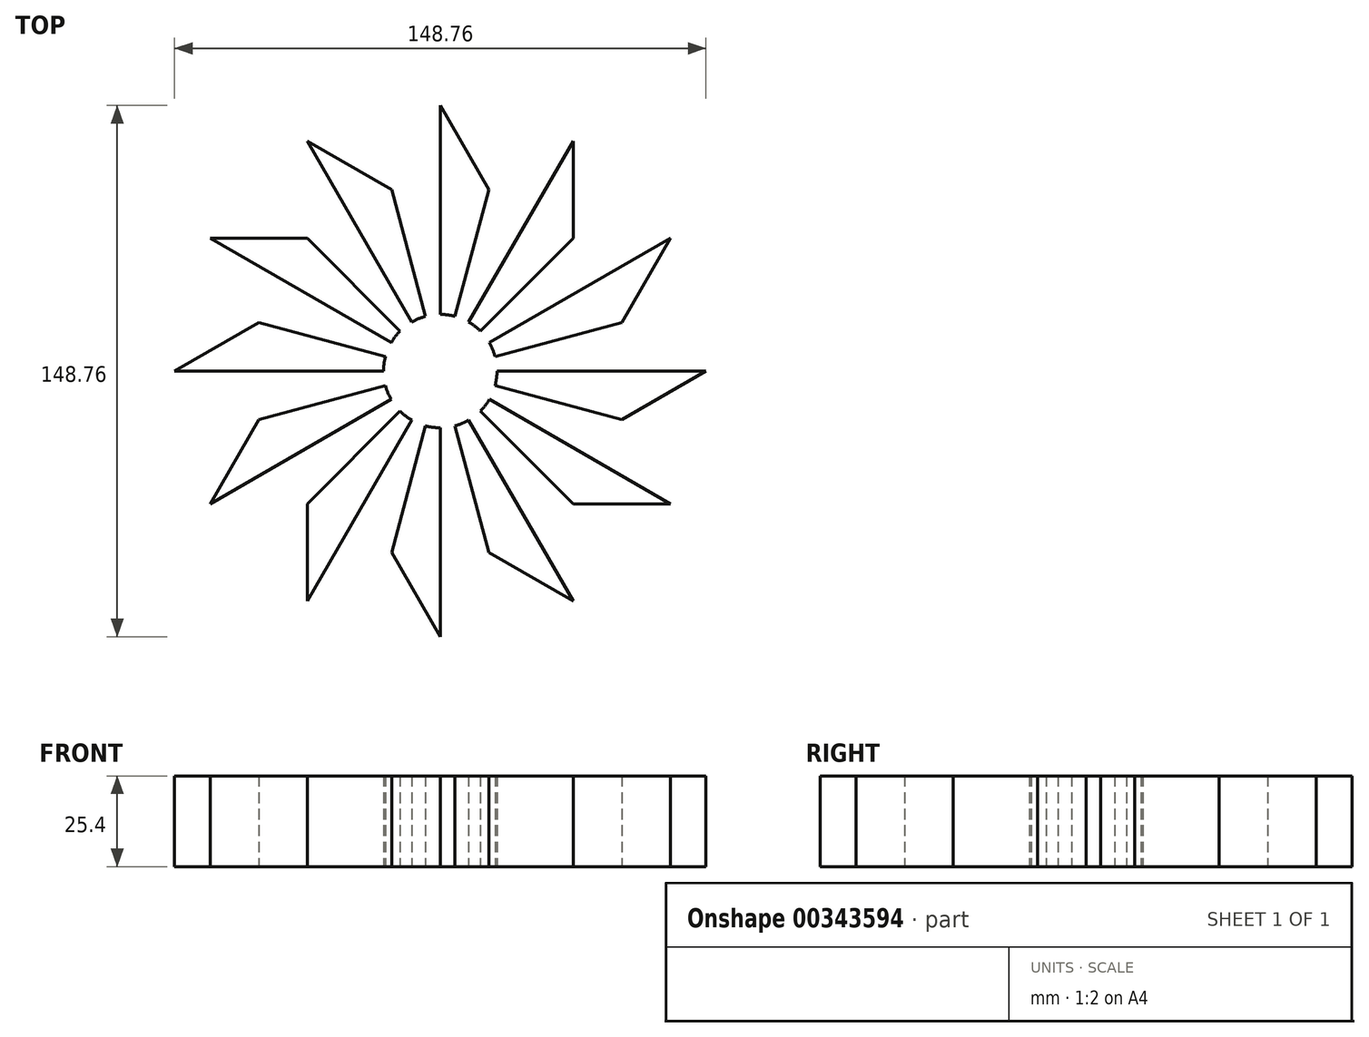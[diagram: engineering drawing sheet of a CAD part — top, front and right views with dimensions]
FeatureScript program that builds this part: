
annotation { "Feature Type Name" : "Feature", "Feature Type Description" : "" }
export const myFeature = defineFeature(function(context is Context, id is Id, definition is map)
    precondition{}
    {
        {
            var Q0;
            Q0=qCreatedBy(makeId("Top.planeOp"),FACE);
            var sketch = newSketch(context, id + "F0", { "sketchPlane" : qUnion([Q0])});
            skLineSegment(sketch, "E0", {"start": v(15.33, 4.1) * mm, "end": v(50.8, 13.61) * mm});
            skLineSegment(sketch, "E1", {"start": v(50.8, 13.61) * mm, "end": v(74.38, 0) * mm});
            skLineSegment(sketch, "E2.MirrorCS", {"start": v(50.8, -13.61) * mm, "end": v(74.38, 0) * mm});
            skLineSegment(sketch, "E3", {"start": v(15.87, 0) * mm, "end": v(74.38, 0) * mm});
            skLineSegment(sketch, "E4.1.0", {"start": v(50.8, 13.61) * mm, "end": v(64.41, 37.19) * mm});
            skLineSegment(sketch, "E4.1.1", {"start": v(13.75, 7.94) * mm, "end": v(64.41, 37.19) * mm});
            skLineSegment(sketch, "E4.1.2", {"start": v(37.19, 37.19) * mm, "end": v(64.41, 37.19) * mm});
            skLineSegment(sketch, "E4.1.3", {"start": v(11.23, 11.23) * mm, "end": v(37.19, 37.19) * mm});
            skLineSegment(sketch, "E4.2.0", {"start": v(37.19, 37.19) * mm, "end": v(37.19, 64.41) * mm});
            skLineSegment(sketch, "E4.2.1", {"start": v(7.94, 13.75) * mm, "end": v(37.19, 64.41) * mm});
            skLineSegment(sketch, "E4.2.2", {"start": v(13.61, 50.8) * mm, "end": v(37.19, 64.41) * mm});
            skLineSegment(sketch, "E4.2.3", {"start": v(4.1, 15.33) * mm, "end": v(13.61, 50.8) * mm});
            skLineSegment(sketch, "E4.3.0", {"start": v(13.61, 50.8) * mm, "end": v(0, 74.38) * mm});
            skLineSegment(sketch, "E4.3.1", {"start": v(0, 15.87) * mm, "end": v(0, 74.38) * mm});
            skLineSegment(sketch, "E4.3.2", {"start": v(-13.61, 50.8) * mm, "end": v(0, 74.38) * mm});
            skLineSegment(sketch, "E4.3.3", {"start": v(-4.1, 15.33) * mm, "end": v(-13.61, 50.8) * mm});
            skLineSegment(sketch, "E4.4.0", {"start": v(-13.61, 50.8) * mm, "end": v(-37.19, 64.41) * mm});
            skLineSegment(sketch, "E4.4.1", {"start": v(-7.94, 13.75) * mm, "end": v(-37.19, 64.41) * mm});
            skLineSegment(sketch, "E4.4.2", {"start": v(-37.19, 37.19) * mm, "end": v(-37.19, 64.41) * mm});
            skLineSegment(sketch, "E4.4.3", {"start": v(-11.23, 11.23) * mm, "end": v(-37.19, 37.19) * mm});
            skLineSegment(sketch, "E4.5.0", {"start": v(-37.19, 37.19) * mm, "end": v(-64.41, 37.19) * mm});
            skLineSegment(sketch, "E4.5.1", {"start": v(-13.75, 7.94) * mm, "end": v(-64.41, 37.19) * mm});
            skLineSegment(sketch, "E4.5.2", {"start": v(-50.8, 13.61) * mm, "end": v(-64.41, 37.19) * mm});
            skLineSegment(sketch, "E4.5.3", {"start": v(-15.33, 4.1) * mm, "end": v(-50.8, 13.61) * mm});
            skLineSegment(sketch, "E4.6.0", {"start": v(-50.8, 13.61) * mm, "end": v(-74.38, 0) * mm});
            skLineSegment(sketch, "E4.6.1", {"start": v(-15.88, 0) * mm, "end": v(-74.38, 0) * mm});
            skLineSegment(sketch, "E4.6.2", {"start": v(-50.8, -13.61) * mm, "end": v(-74.38, 0) * mm});
            skLineSegment(sketch, "E4.6.3", {"start": v(-15.33, -4.1) * mm, "end": v(-50.8, -13.61) * mm});
            skLineSegment(sketch, "E4.7.0", {"start": v(-50.8, -13.61) * mm, "end": v(-64.41, -37.19) * mm});
            skLineSegment(sketch, "E4.7.1", {"start": v(-13.75, -7.94) * mm, "end": v(-64.41, -37.19) * mm});
            skLineSegment(sketch, "E4.7.2", {"start": v(-37.19, -37.19) * mm, "end": v(-64.41, -37.19) * mm});
            skLineSegment(sketch, "E4.7.3", {"start": v(-11.23, -11.23) * mm, "end": v(-37.19, -37.19) * mm});
            skLineSegment(sketch, "E4.8.0", {"start": v(-37.19, -37.19) * mm, "end": v(-37.19, -64.41) * mm});
            skLineSegment(sketch, "E4.8.1", {"start": v(-7.94, -13.75) * mm, "end": v(-37.19, -64.41) * mm});
            skLineSegment(sketch, "E4.8.2", {"start": v(-13.61, -50.8) * mm, "end": v(-37.19, -64.41) * mm});
            skLineSegment(sketch, "E4.8.3", {"start": v(-4.1, -15.33) * mm, "end": v(-13.61, -50.8) * mm});
            skLineSegment(sketch, "E4.9.0", {"start": v(-13.61, -50.8) * mm, "end": v(0, -74.38) * mm});
            skLineSegment(sketch, "E4.9.1", {"start": v(0, -15.88) * mm, "end": v(0, -74.38) * mm});
            skLineSegment(sketch, "E4.9.2", {"start": v(13.61, -50.8) * mm, "end": v(0, -74.38) * mm});
            skLineSegment(sketch, "E4.9.3", {"start": v(4.1, -15.33) * mm, "end": v(13.61, -50.8) * mm});
            skLineSegment(sketch, "E4.10.0", {"start": v(13.61, -50.8) * mm, "end": v(37.19, -64.41) * mm});
            skLineSegment(sketch, "E4.10.1", {"start": v(7.94, -13.75) * mm, "end": v(37.19, -64.41) * mm});
            skLineSegment(sketch, "E4.10.2", {"start": v(37.19, -37.19) * mm, "end": v(37.19, -64.41) * mm});
            skLineSegment(sketch, "E4.10.3", {"start": v(11.23, -11.23) * mm, "end": v(37.19, -37.19) * mm});
            skLineSegment(sketch, "E4.11.0", {"start": v(37.19, -37.19) * mm, "end": v(64.41, -37.19) * mm});
            skLineSegment(sketch, "E4.11.1", {"start": v(13.75, -7.94) * mm, "end": v(64.41, -37.19) * mm});
            skLineSegment(sketch, "E4.11.2", {"start": v(50.8, -13.61) * mm, "end": v(64.41, -37.19) * mm});
            skLineSegment(sketch, "E4.11.3", {"start": v(15.33, -4.1) * mm, "end": v(50.8, -13.61) * mm});
            skPoint(sketch, "E4.center", {"position": v(0, 0) * mm});
            skCircle(sketch, "E5", {"center": v(0, 0) * mm, "radius": 15.88 * mm});
            skSolve(sketch);
        }
        {
            var Q0;
            {var subQ0=sQuery(id+"F0.wireOp",EDGE,"E4.4.3");Q0=makeQuery(id+"F0.imprint","IMPRINT",FACE,{"disambiguationData":[TD([[makeQuery(id+"F0.imprint","IMPRINT",EDGE,{"derivedFrom":subQ0}),1.0]])]});}
            var Q1;
            {var subQ0=sQuery(id+"F0.wireOp",EDGE,"E4.3.3");Q1=makeQuery(id+"F0.imprint","IMPRINT",FACE,{"disambiguationData":[TD([[makeQuery(id+"F0.imprint","IMPRINT",EDGE,{"derivedFrom":subQ0}),1.0]])]});}
            var Q2;
            {var subQ0=sQuery(id+"F0.wireOp",EDGE,"E4.2.3");Q2=makeQuery(id+"F0.imprint","IMPRINT",FACE,{"disambiguationData":[TD([[makeQuery(id+"F0.imprint","IMPRINT",EDGE,{"derivedFrom":subQ0}),1.0]])]});}
            var Q3;
            {var subQ0=sQuery(id+"F0.wireOp",EDGE,"E4.1.3");Q3=makeQuery(id+"F0.imprint","IMPRINT",FACE,{"disambiguationData":[TD([[makeQuery(id+"F0.imprint","IMPRINT",EDGE,{"derivedFrom":subQ0}),1.0]])]});}
            var Q4;
            {var subQ0=sQuery(id+"F0.wireOp",EDGE,"E0");Q4=makeQuery(id+"F0.imprint","IMPRINT",FACE,{"disambiguationData":[TD([[makeQuery(id+"F0.imprint","IMPRINT",EDGE,{"derivedFrom":subQ0}),1.0]])]});}
            var Q5;
            Q5=makeQuery(id+"F0.imprint","IMPRINT",FACE,{"disambiguationData":[TD([[makeQuery(id+"F0.imprint","IMPRINT",EDGE,{"derivedFrom":sQuery(id+"F0.wireOp",EDGE,"E2.MirrorCS")}),1.0]])]});
            var Q6;
            {var subQ0=sQuery(id+"F0.wireOp",EDGE,"E4.10.3");Q6=makeQuery(id+"F0.imprint","IMPRINT",FACE,{"disambiguationData":[TD([[makeQuery(id+"F0.imprint","IMPRINT",EDGE,{"derivedFrom":subQ0}),1.0]])]});}
            var Q7;
            {var subQ0=sQuery(id+"F0.wireOp",EDGE,"E4.9.3");Q7=makeQuery(id+"F0.imprint","IMPRINT",FACE,{"disambiguationData":[TD([[makeQuery(id+"F0.imprint","IMPRINT",EDGE,{"derivedFrom":subQ0}),1.0]])]});}
            var Q8;
            {var subQ0=sQuery(id+"F0.wireOp",EDGE,"E4.8.3");Q8=makeQuery(id+"F0.imprint","IMPRINT",FACE,{"disambiguationData":[TD([[makeQuery(id+"F0.imprint","IMPRINT",EDGE,{"derivedFrom":subQ0}),1.0]])]});}
            var Q9;
            {var subQ0=sQuery(id+"F0.wireOp",EDGE,"E4.7.3");Q9=makeQuery(id+"F0.imprint","IMPRINT",FACE,{"disambiguationData":[TD([[makeQuery(id+"F0.imprint","IMPRINT",EDGE,{"derivedFrom":subQ0}),1.0]])]});}
            var Q10;
            {var subQ0=sQuery(id+"F0.wireOp",EDGE,"E4.6.3");Q10=makeQuery(id+"F0.imprint","IMPRINT",FACE,{"disambiguationData":[TD([[makeQuery(id+"F0.imprint","IMPRINT",EDGE,{"derivedFrom":subQ0}),1.0]])]});}
            var Q11;
            {var subQ0=sQuery(id+"F0.wireOp",EDGE,"E4.5.3");Q11=makeQuery(id+"F0.imprint","IMPRINT",FACE,{"disambiguationData":[TD([[makeQuery(id+"F0.imprint","IMPRINT",EDGE,{"derivedFrom":subQ0}),1.0]])]});}
            extrude(context, id + "F1", {"entities" : qUnion([Q0, Q1, Q2, Q3, Q4, Q5, Q6, Q7, Q8, Q9, Q10, Q11]), "depth" : 25.4 * mm});
        }
    });
